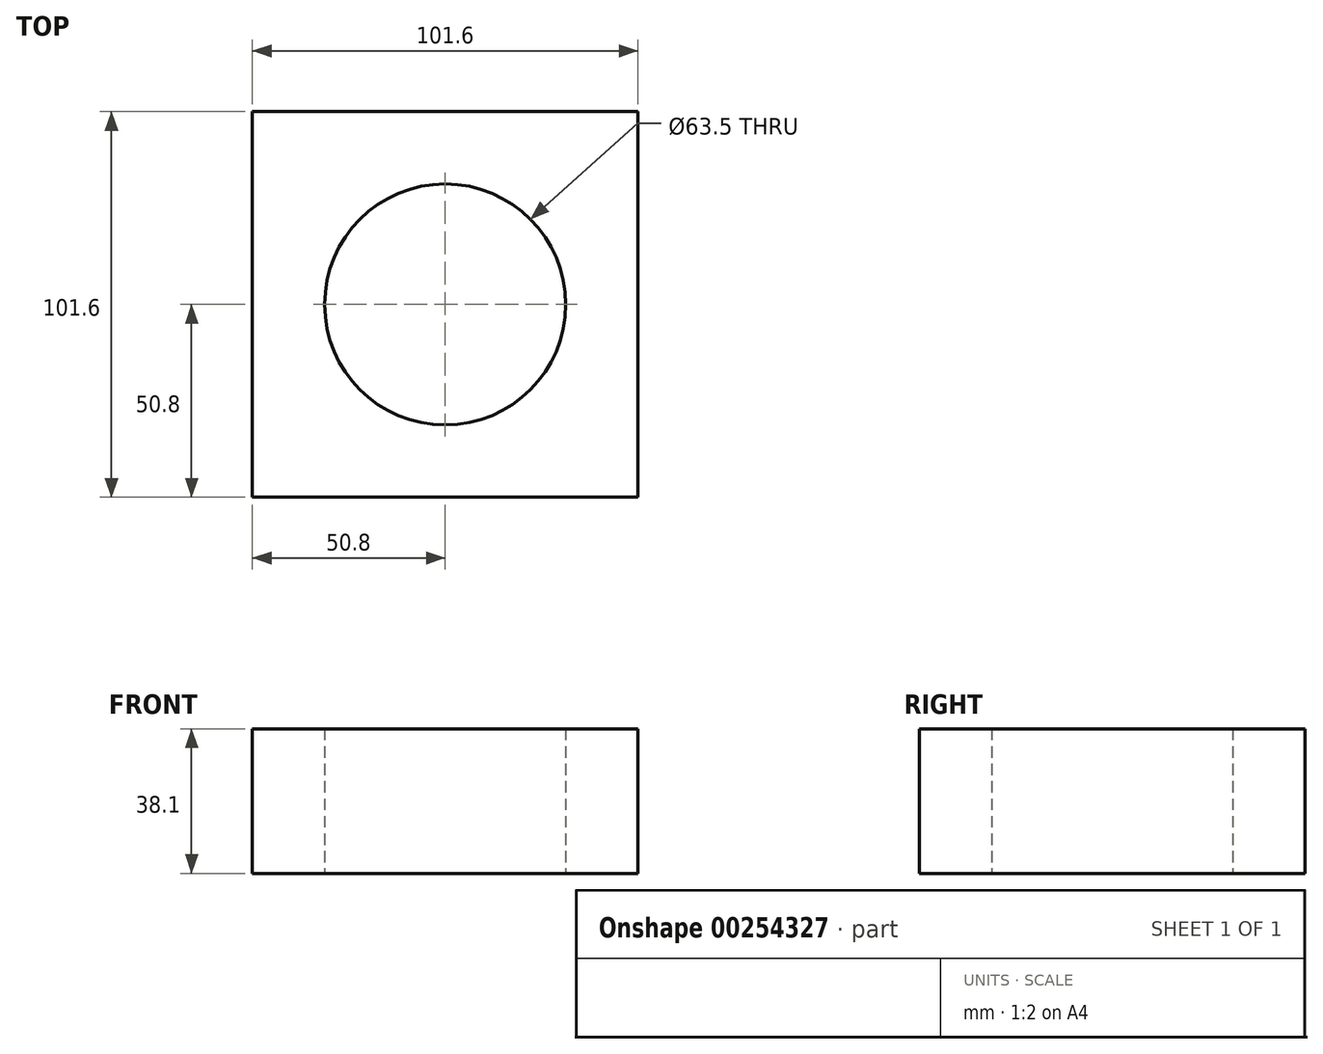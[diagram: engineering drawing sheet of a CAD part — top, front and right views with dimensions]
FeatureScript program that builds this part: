
annotation { "Feature Type Name" : "Feature", "Feature Type Description" : "" }
export const myFeature = defineFeature(function(context is Context, id is Id, definition is map)
    precondition{}
    {
        {
            var Q0;
            Q0=qCreatedBy(makeId("Top.planeOp"),FACE);
            var sketch = newSketch(context, id + "F0", { "sketchPlane" : qUnion([Q0])});
            skLineSegment(sketch, "E0.bottom", {"start": v(-50.8, -50.8) * mm, "end": v(50.8, -50.8) * mm});
            skLineSegment(sketch, "E0.top", {"start": v(-50.8, 50.8) * mm, "end": v(50.8, 50.8) * mm});
            skLineSegment(sketch, "E0.left", {"start": v(-50.8, -50.8) * mm, "end": v(-50.8, 50.8) * mm});
            skLineSegment(sketch, "E0.right", {"start": v(50.8, -50.8) * mm, "end": v(50.8, 50.8) * mm});
            skPoint(sketch, "E0.middle", {"position": v(0, 0) * mm});
            skCircle(sketch, "E1", {"center": v(0, 0) * mm, "radius": 31.75 * mm});
            skLineSegment(sketch, "E2.bottom", {"start": v(-76.2, -76.2) * mm, "end": v(76.2, -76.2) * mm});
            skLineSegment(sketch, "E2.top", {"start": v(-76.2, 76.2) * mm, "end": v(76.2, 76.2) * mm});
            skLineSegment(sketch, "E2.left", {"start": v(-76.2, -76.2) * mm, "end": v(-76.2, 76.2) * mm});
            skLineSegment(sketch, "E2.right", {"start": v(76.2, -76.2) * mm, "end": v(76.2, 76.2) * mm});
            skSolve(sketch);
        }
        {
            var Q0;
            Q0=makeQuery(id+"F0.imprint","IMPRINT",FACE,{"disambiguationData":[TD([[makeQuery(id+"F0.imprint","IMPRINT",EDGE,{"derivedFrom":sQuery(id+"F0.wireOp",EDGE,"E0.bottom")}),1.0]])]});
            extrude(context, id + "F1", {"entities" : qUnion([Q0]), "depth" : 38.1 * mm});
        }
    });
